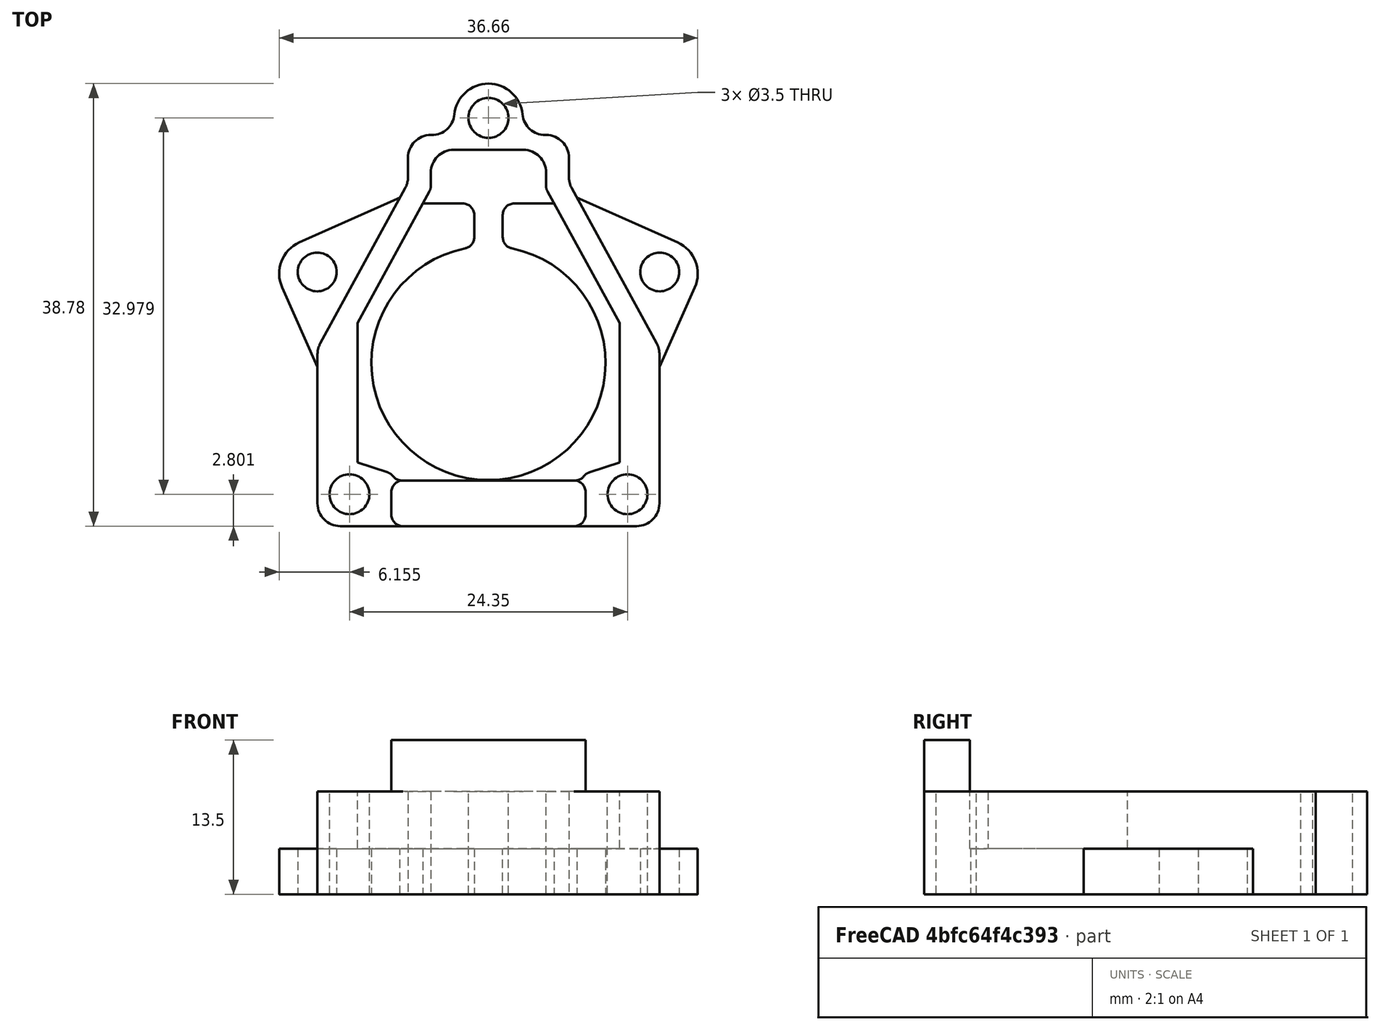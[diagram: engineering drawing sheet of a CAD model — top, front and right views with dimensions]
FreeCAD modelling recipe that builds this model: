
FCSTD DOCUMENT  (FreeCAD 0.14R3692 (Git))
Label: UpperHorizontalMount
License: CC-BY 3.0
LicenseURL: http://creativecommons.org/licenses/by/3.0/
objects: Part::Cut×3, Part::Box×2, Part::Cylinder×2, Part::Fillet×2, Part::Fuse×2, Part::Feature×1, Part::Mirroring×1, App::DocumentObjectGroup×1
note: 13 computed .brp shape members not serialized (recipe doc carries the construction recipe); baked Part::Feature solids carry a one-line shape summary decoded from their .brp

FEATURE [Part::Feature] Part__Feature  label="UpperVerticalMount"
  shape: bbox 29.95 x 38.78 x 13.5 mm, 60 faces (baked)
FEATURE [Part::Box] Box  label="Cube"
  Height = 4
  Length = 14
  Placement = pos=(-14,5.5,5.3) rot=(0,0,1;0.418879rad)
  Width = 13
FEATURE [Part::Cylinder] Cylinder
  Angle = 360
  Height = 17
  Placement = pos=(-15,16,0) rot=(0,0,1;0rad)
  Radius = 1.7
FEATURE [Part::Box] Box001  label="Cube001"
  Height = 13
  Length = 23
  Placement = pos=(-5,-2.5,-0.7) rot=(0,0,1;1.0821rad)
  Width = 13
FEATURE [Part::Cut] Cut
  Base = -> Box
  Tool = -> Box001
FEATURE [Part::Fillet] Fillet
  Base = -> Cut
  Edges = 1 edges r=3: [Edge2]
FEATURE [Part::Cut] Cut001
  Base = -> Fillet
  Tool = -> Cylinder
FEATURE [Part::Mirroring] Part__Mirroring  label="Cut001 (Mirror #1)"
  Base = (0,0,0)
  Normal = (1,0,0)
  Source = -> Cut001
FEATURE [Part::Fillet] Fillet001
  Base = -> Cut
  Edges = 1 edges r=3: [Edge2]
FEATURE [Part::Cylinder] Cylinder002
  Angle = 360
  Height = 17
  Placement = pos=(-15,16,0) rot=(0,0,1;0rad)
  Radius = 1.7
FEATURE [Part::Cut] Cut002
  Base = -> Fillet001
  Tool = -> Cylinder002
FEATURE [Part::Fuse] Fusion
  Base = -> Part__Feature
  Tool = -> Part__Mirroring
FEATURE [Part::Fuse] Fusion001  label="UpperHorizontalMount"
  Base = -> Cut002
  Placement = pos=(0,0,0) rot=(0,1,0;3.14159rad)
  Tool = -> Fusion
FEATURE [App::DocumentObjectGroup] Group  label="Working"
  Group = -> [Cut]
